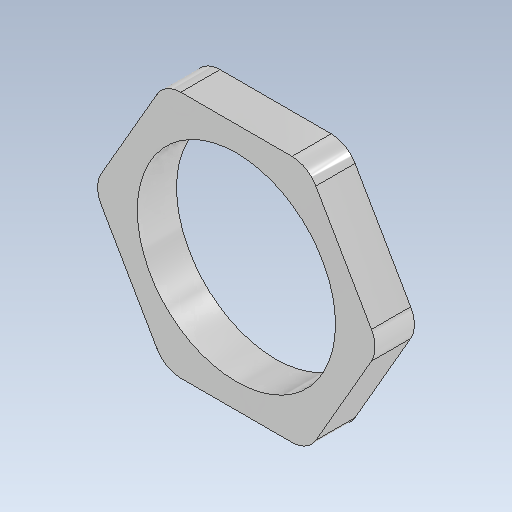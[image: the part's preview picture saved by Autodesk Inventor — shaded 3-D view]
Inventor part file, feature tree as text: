
AUTODESK INVENTOR PART (.ipt)
format: ipt  version: 2021 (Build 250183000, 183)  size: 118,784 bytes
history: native  units: mm
features: extrude x1, fillet x1, sketch x1
ambient origin geometry x8: Origin, YZ Plane, XZ Plane, XY Plane, X Axis, Y Axis, Z Axis, Center Point
bodies: Solid1 (feature_tree)
feature tree (3):
  extrude  "Extrusion1"  Depth=2.0mm
  fillet  "Fillet1"  Radius=2.85mm
  sketch  "Sketch1"  dims[d0=18.0mm d1=14.4mm d2=2.85mm d3=0.0mm d4=2.0mm]
